# Revit family: 3-109-xx Juno Fan
name_source: partatom
category: Generic Models
revit_build: Autodesk Revit 2018 (Build: 20170223_1515(x64)
units: mm (PartAtom-declared; Revit-internal decimal feet)

## family parameters
Always vertical = Yes
Can host rebar = No
Cut with Voids When Loaded = No
Host = Ceiling
Part Type = Normal
Room Calculation Point = No
Round Connector Dimension = Use Diameter
Shared = No

## types (19) — shared parameters
Main Diffuser = Matte White Acrylic
Manufacturer = Oxygen - Lighting & Fans
Model = 3-109-xx/37-109-xx Juno Fan
References = Ref. 3 = 120 V / Ref. 37 = 277 V
URL = www.oxygenlighting.com
Voltage Input = 120 V or 277 V - 50/60 Hz

## per-type parameters (varying)
| type | Blade Finish | Metal Finish | Voltage |
| 3-109-15 / Black - Black Blades | 15 - Black | 15 - Black | 120 V |
| 3-109-15 / Black - Weathered Gray Blades | Weathered Gray Blades | 15 - Black | 120 V |
| 3-109-22 / Oiled Bronze - Oiled Bronze Blades | 22- Oiled Bronze | 22- Oiled Bronze | 120 V |
| 3-109-22 / Oiled Bronze - Weathered Oak Blades | Weathered Oak | 22- Oiled Bronze | 120 V |
| 3-109-24 / Satin Nickel - Satin Nicke Blades | 24 - Satin Nickel | 24 - Satin Nickel | 120 V |
| 3-109-24 / Satin Nickel - Weathered Gray Blades | Weathered Gray Blades | 24 - Satin Nickel | 120 V |
| 3-109-40 / Aged Brass - Aged Brass Blades | 40 - Aged Brass | 40 - Aged Brass | 120 V |
| 3-109-40 / Aged Brass - Weathered Oak Blades | Weathered Oak | 40 - Aged Brass | 120 V |
| 3-109-6 / White - White Blades | 6 - White | 6 - White | 120 V |
| 37-109-15 / Black - Black Blades | 15 - Black | 15 - Black | 277 V |
| 37-109-15 / Black - Weathered Gray Blades | Weathered Gray Blades | 15 - Black | 277 V |
| 37-109-22 / Oiled Bronze - Oiled Bronze Blades | 22- Oiled Bronze | 22- Oiled Bronze | 277 V |
| 37-109-22 / Oiled Bronze - Weathered Oak Blades | Weathered Oak | 22- Oiled Bronze | 277 V |
| 37-109-24 / Satin Nickel - Satin Nicke Blades | 24 - Satin Nickel | 24 - Satin Nickel | 277 V |
| 37-109-24 / Satin Nickel - Weathered Gray Blades | Weathered Gray Blades | 24 - Satin Nickel | 277 V |
| 37-109-40 / Aged Brass - Aged Brass Blades | 40 - Aged Brass | 40 - Aged Brass | 277 V |
| 37-109-40 / Aged Brass - Weathered Oak Blades | Weathered Oak | 40 - Aged Brass | 277 V |
| 37-109-6 / White - White Blades | 6 - White | 6 - White | 277 V |
| 37-109-24 / Satin Nickel - Satin Nickel Blades | 24 - Satin Nickel | 24 - Satin Nickel | 277 V |

## geometry (parser evidence)
native form markers: Blend x2, Sweep x8
no freeform markers — native parametric forms only
